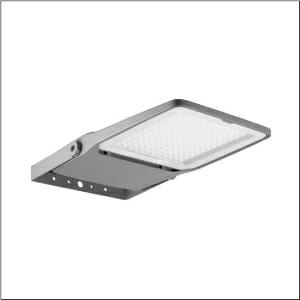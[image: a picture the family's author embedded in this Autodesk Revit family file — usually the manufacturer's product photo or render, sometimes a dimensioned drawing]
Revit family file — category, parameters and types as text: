
# Revit family: floodlight_fl_20_midi___pl52_5xa7682d2d2ac_d313
name_source: partatom
category: Lighting Fixtures
units: mm (PartAtom-declared; Revit-internal decimal feet)

## family parameters
Cut with Voids When Loaded = No
Host = Face
Light Source = No
Part Type = Normal
Room Calculation Point = No
Round Connector Dimension = Use Diameter
Shared = No

## types (1)
- --- (1 x LED 4000K / CRI = 70 (unbekannt), 17990 lm, 4000K)
    Apparent Load = 142 VA
    CIE Flux Codes = 27 59 98 100 100
    Color Rendering = 70
    Color Temperature = 4000K
    Default Elevation = 1800 mm
    Description = Floodlight FL 20 midi, floodlight, primary light control with lens, of plastic, primary optical cover: protective disc, of toughened safety glass, transparent, light distribution: PL52, light emission: direct distribution, primary light characteristic: asymmetric, installation type: surface-mounted, LED, High Power LED, rated luminous flux: 17.990lm, luminous efficacy: 127lm/W, light colour: 740, colour temperature: 4000K, control gear: ECG Plus, control: flexible luminous flux parameterisation, time-dependent luminous flux control, digital communication interface, power reduction, overheat protection, electronic power reduction, with terminal, 5-pole, max. 2.5mm², mains connection: 220..240V, AC, 50/60Hz, rated input power: 142W, LED unit, of diecast aluminium, powder-coated, Siteco® metallic grey (DB 702S), corrosivity category C5 mid according to DIN EN ISO 12944, incl. 1x M20 cable gland for cable Ø 6.5..12mm, length: 731mm, width: 450mm, height: 76mm, housing frame, of diecast aluminium, powder-coated, Siteco® metallic grey (DB 702S), wall fastening, of steel, powder-coated, Siteco® metallic grey (DB 702S), DALI, protection rating (complete): IP66, insulation class (complete): insulation class II (safety insulation), certification: CE, ENEC, VDE, protection symbol: D, permissible operating ambient temperature: -40..+40°C, permissible operating ambient temperature for outdoor applications: -40..+50°C, standard: DIN EN 12944, packaging unit: 1 piece

Light Distribution: PL52
    Height = 76 mm
    Lamp = 1 x LED 4000K / CRI >= 70 (unbekannt)
    Lamp Light Flux = 17990 lm
    Lamp count = 1
    Length = 731 mm
    Luminous efficacy = 127 lm/W
    Manufacturer = Siteco
    ModVariant = No
    Model = 5XA7682D2D2AC
    Mounting Place = Wall
    Mounting Type = Surface mounted
    Number of Poles = 1
    OnlyDefault = Yes
    Power Factor = 1
    Product Name = Floodlight FL 20 midi | PL52
    Product group = floodlight | wall mounted
    ProductGroupID = 2001
    Protection Class = Protection class II
    Protection Degree = IP 66
    RLX_Detail_Level = 1
    RLX_Emergency_Light_Flux = 0 lm
    RLX_Emergency_Type = 0
    RLX_Emergency_Type_DB = No
    RlxData = <blob elided: 92173 chars, md5=274a010c>
    Socket = socket
    Standby Power = 0 W
    System Light Flux = 17990 lm
    System Power = 142 W
    Type Comments = factory setting: luminous flux: 100 % | dim-lin: 254 | 489 mA
    Type Image = l_1005944.jpg
    URL = http://relux.com
    VarID = @adj_147895
    Voltage = 0 V
    Weight = 0.00 kg
    Width = 450 mm

## geometry (parser evidence)
native form markers: Blend x4, Sweep x14
no freeform markers — native parametric forms only
